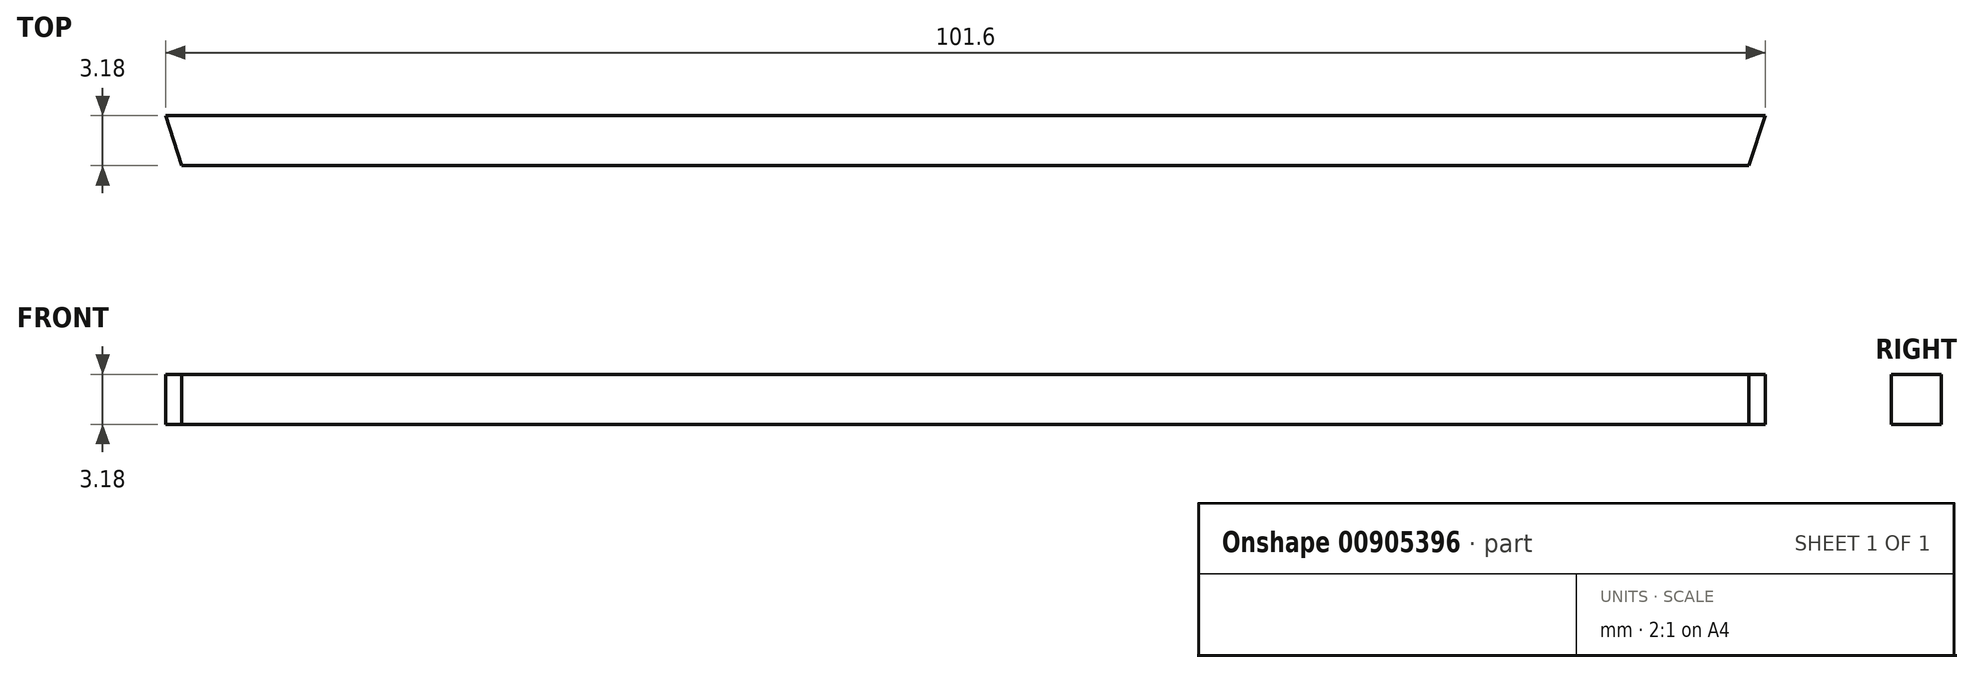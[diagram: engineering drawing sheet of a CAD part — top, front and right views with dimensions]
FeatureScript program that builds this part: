
annotation { "Feature Type Name" : "Feature", "Feature Type Description" : "" }
export const myFeature = defineFeature(function(context is Context, id is Id, definition is map)
    precondition{}
    {
        {
            var Q0;
            Q0=qCreatedBy(makeId("Front.planeOp"),FACE);
            var sketch = newSketch(context, id + "F0", { "sketchPlane" : qUnion([Q0])});
            skLineSegment(sketch, "E0.bottom", {"start": v(-89.05, -2.46) * mm, "end": v(12.55, -2.46) * mm});
            skLineSegment(sketch, "E0.top", {"start": v(-89.05, -5.64) * mm, "end": v(12.55, -5.64) * mm});
            skLineSegment(sketch, "E0.left", {"start": v(-89.05, -2.46) * mm, "end": v(-89.05, -5.64) * mm});
            skLineSegment(sketch, "E0.right", {"start": v(12.55, -2.46) * mm, "end": v(12.55, -5.64) * mm});
            skSolve(sketch);
        }
        {
            var Q0;
            Q0=makeQuery(id+"F0.imprint","IMPRINT",FACE,{"disambiguationData":[TD([[makeQuery(id+"F0.imprint","IMPRINT",EDGE,{"derivedFrom":sQuery(id+"F0.wireOp",EDGE,"E0.bottom")}),-1.0]])]});
            extrude(context, id + "F1", {"entities" : qUnion([Q0]), "depth" : 3.17 * mm, "offsetDistance" : 25.4 * mm});
        }
        {
            var Q0;
            Q0=makeQuery(id+"F1.opExtrude","CAP_EDGE",EDGE,{"disambiguationData":[OSD([sQuery(id+"F0.wireOp",EDGE,"E0.left")])],"isStart":false});
            chamfer(context, id + "F2", {"entities" : qUnion([Q0]), "chamferType" : ChamferType.OFFSET_ANGLE, "width" : 3.17 * mm, "oppositeDirection" : true, "angle" : 18 * degree, "tangentPropagation" : true});
        }
        {
            var Q0;
            Q0=makeQuery(id+"F1.opExtrude","CAP_EDGE",EDGE,{"disambiguationData":[OSD([sQuery(id+"F0.wireOp",EDGE,"E0.right")])],"isStart":false});
            chamfer(context, id + "F3", {"entities" : qUnion([Q0]), "chamferType" : ChamferType.OFFSET_ANGLE, "width" : 3.17 * mm, "oppositeDirection" : false, "angle" : 18 * degree, "tangentPropagation" : true});
        }
    });
